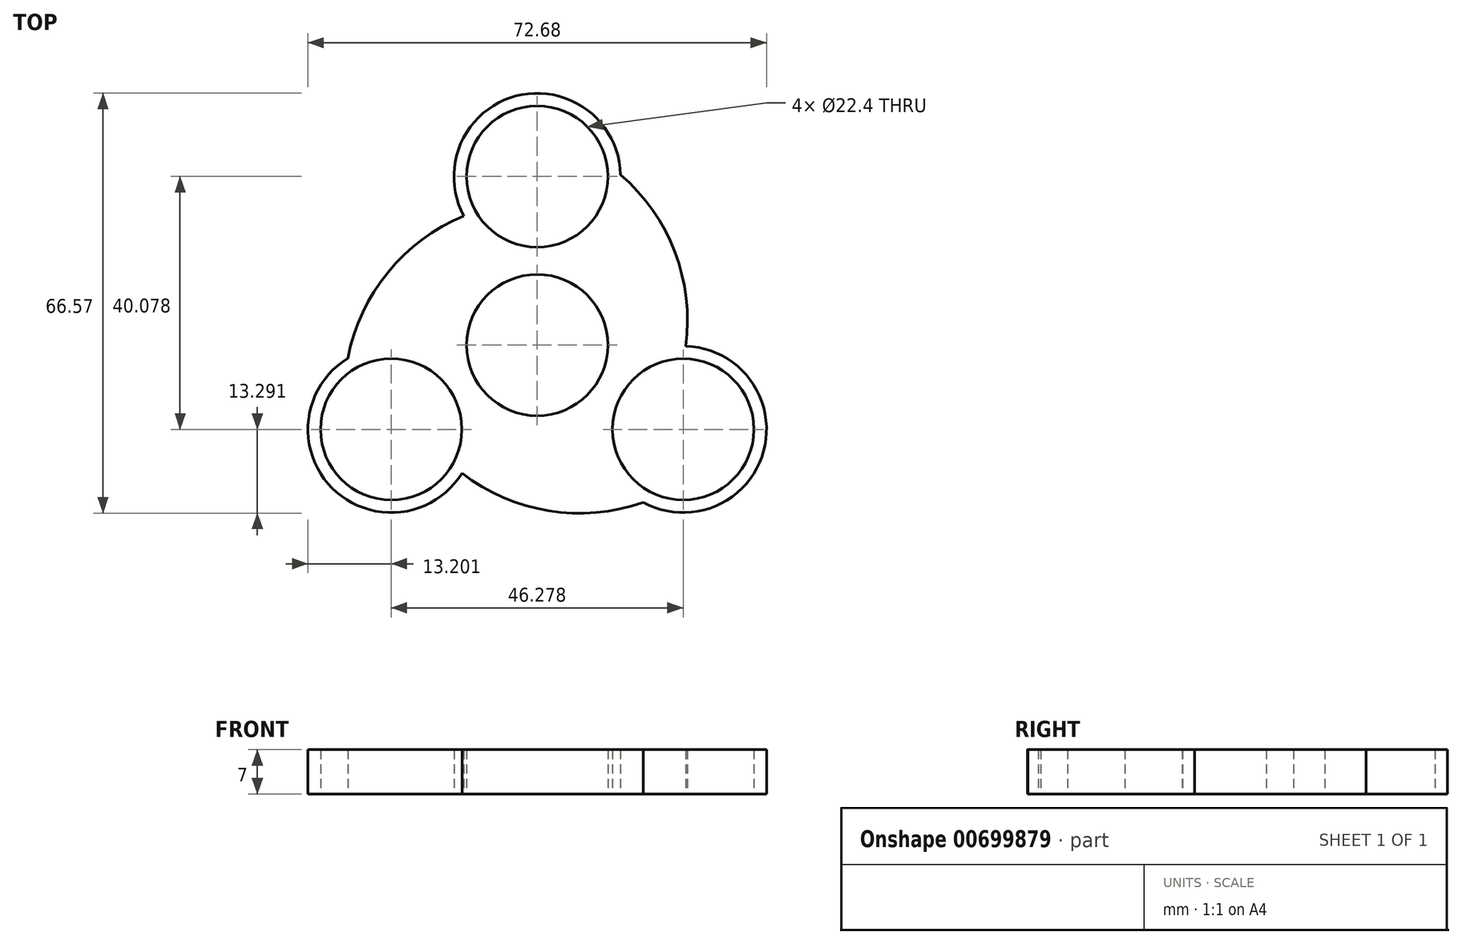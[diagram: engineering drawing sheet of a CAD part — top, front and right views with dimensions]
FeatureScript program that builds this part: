
annotation { "Feature Type Name" : "Feature", "Feature Type Description" : "" }
export const myFeature = defineFeature(function(context is Context, id is Id, definition is map)
    precondition{}
    {
        {
            var Q0;
            Q0=qCreatedBy(makeId("Top.planeOp"),FACE);
            var sketch = newSketch(context, id + "F0", { "sketchPlane" : qUnion([Q0])});
            skCircle(sketch, "E0", {"center": v(0, 0) * mm, "radius": 11.2 * mm});
            skCircle(sketch, "E1", {"center": v(0, 26.72) * mm, "radius": 11.2 * mm});
            skArc(sketch, "E2", {"start": v(13.2, 27.03) * mm, "mid": v(-3.38, 39.48) * mm, "end": v(-11.62, 20.46) * mm});
            skArc(sketch, "E3.1.0", {"start": v(-30, -2.08) * mm, "mid": v(-32.5, -22.66) * mm, "end": v(-11.9, -20.3) * mm});
            skArc(sketch, "E3.2.0", {"start": v(16.8, -24.94) * mm, "mid": v(35.88, -16.82) * mm, "end": v(23.53, -0.17) * mm});
            skCircle(sketch, "E4.1.0", {"center": v(-23.14, -13.36) * mm, "radius": 11.2 * mm});
            skCircle(sketch, "E4.2.0", {"center": v(23.14, -13.36) * mm, "radius": 11.2 * mm});
            skArc(sketch, "E5", {"start": v(23.53, -0.17) * mm, "mid": v(21.81, 14.74) * mm, "end": v(13.2, 27.03) * mm});
            skArc(sketch, "E6.1.0", {"start": v(-11.62, 20.46) * mm, "mid": v(-23.67, 11.52) * mm, "end": v(-30, -2.08) * mm});
            skArc(sketch, "E6.2.0", {"start": v(-11.9, -20.3) * mm, "mid": v(1.86, -26.26) * mm, "end": v(16.8, -24.94) * mm});
            skSolve(sketch);
        }
        {
            var Q0;
            Q0 = qSketchRegion(id + "F0", true);
            extrude(context, id + "F1", {"entities" : qUnion([Q0]), "depth" : 7 * mm, "offsetDistance" : 25 * mm});
        }
    });
